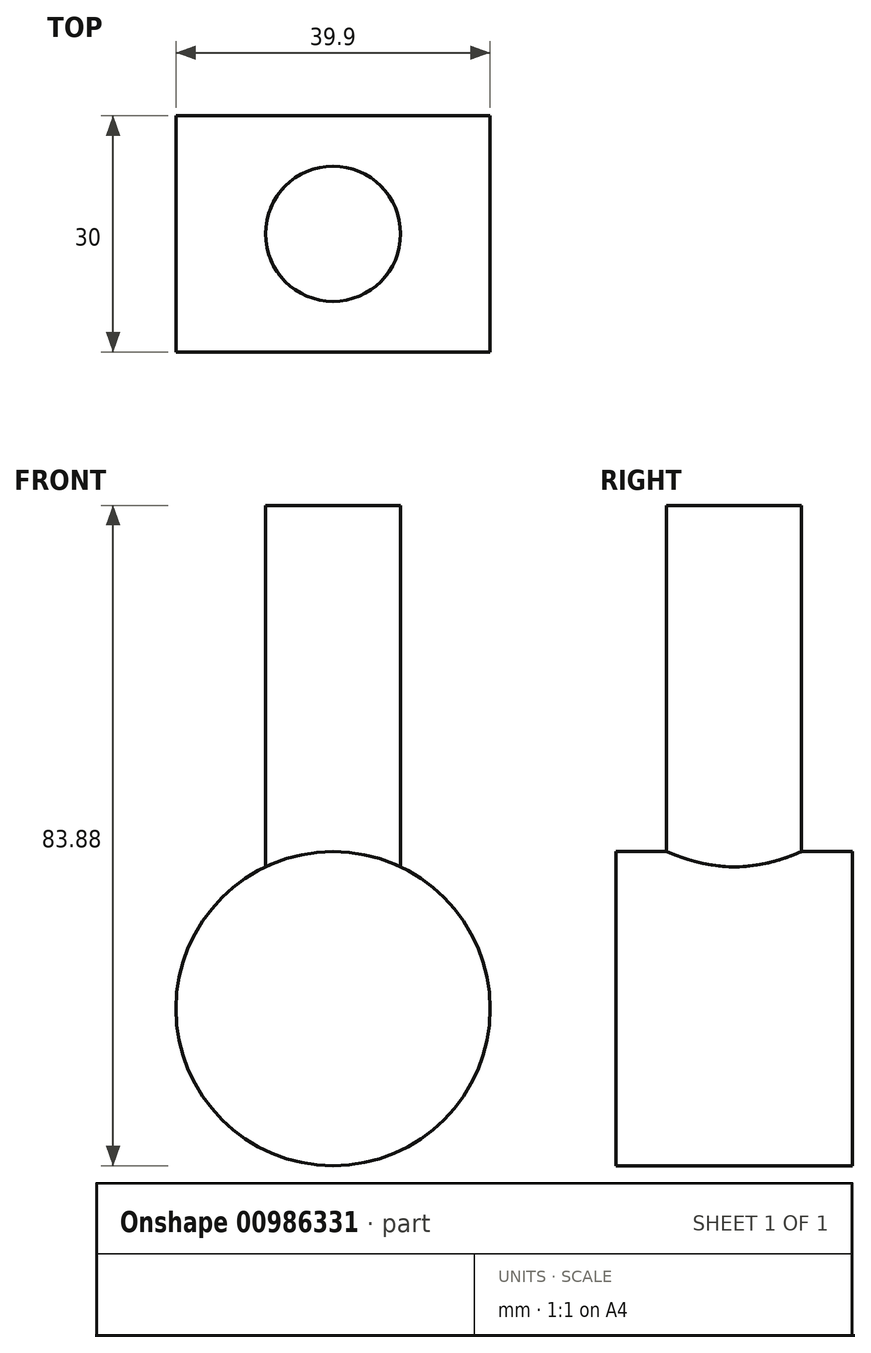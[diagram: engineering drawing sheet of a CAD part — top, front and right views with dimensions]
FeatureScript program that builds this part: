
annotation { "Feature Type Name" : "Feature", "Feature Type Description" : "" }
export const myFeature = defineFeature(function(context is Context, id is Id, definition is map)
    precondition{}
    {
        {
            var Q0;
            Q0=qCreatedBy(makeId("Front.planeOp"),FACE);
            var sketch = newSketch(context, id + "F0", { "sketchPlane" : qUnion([Q0])});
            skCircle(sketch, "E0", {"center": v(0, 0) * mm, "radius": 19.95 * mm});
            skSolve(sketch);
        }
        {
            var Q0;
            Q0 = qSketchRegion(id + "F0", true);
            extrude(context, id + "F1", {"entities" : qUnion([Q0]), "endBound" : BoundingType.SYMMETRIC, "depth" : 30 * mm, "offsetDistance" : 25.4 * mm});
        }
        {
            var Q0;
            Q0=qCreatedBy(makeId("Top.planeOp"),FACE);
            var sketch = newSketch(context, id + "F2", { "sketchPlane" : qUnion([Q0])});
            skCircle(sketch, "E1", {"center": v(0, 0) * mm, "radius": 8.58 * mm});
            skSolve(sketch);
        }
        {
            var Q0;
            Q0 = qSketchRegion(id + "F2", true);
            extrude(context, id + "F3", {"entities" : qUnion([Q0]), "operationType" : NewBodyOperationType.ADD, "endBound" : BoundingType.THROUGH_ALL, "depth" : 25.4 * mm, "offsetDistance" : 25.4 * mm, "hasSecondDirection" : true, "secondDirectionBound" : SecondDirectionBoundingType.UP_TO_NEXT, "secondDirectionOppositeDirection" : true, "secondDirectionDepth" : 25.4 * mm});
        }
    });
